# Revit family: Shower-Receptor-KOHLER-Bellwether-K-9178
name_source: partatom
category: Plumbing Fixtures
revit_build: Autodesk Revit 2015 (Build: 20140606_1530(x64)
units: mm (PartAtom-declared; Revit-internal decimal feet)

## types (6) — shared parameters
ADA Compliant = No
Assembly Code = C1030200
Date Modified = 09/12/2017
Default Elevation = 0"
Description = Bellwether 60inch x 34inch single-threshold shower base with right center drain
Flow Rate = 0 GPM
Height = 4 1/2"
Inlet Connector = Inlet Connection
Length = 60"
Manufacturer = KOHLER Co.
MasterFormat 1995 = 15410
MasterFormat 2004 = 22.41.23
Material = Enameled Cast Iron
Outlet Connector = Outlet Connection
Pressure = 0.00 psi
Product Documentation Link = http://www.us.kohler.com
Product Name = Bellwether
Product Page URL = http://www.us.kohler.com
URL = http://www.us.kohler.com
Waste Connection = Yes
Width = 34"

## per-type parameters (varying)
| type | Finish | Model | Type |
| 0-White | Kohler-Enameled_Cast_Iron-0-White | K-9178-0 | 1 |
| 96-Biscuit | Kohler-Enameled_Cast_Iron-96-Biscuit | K-9178-96 | 2 |
| 47-Almond | Kohler-Enameled_Cast_Iron-47-Almond | K-9178-47 | 3 |
| NY-Dune | Kohler-Enameled_Cast_Iron-NY-Dune | K-9178-NY | 4 |
| 95-Ice Grey | Kohler-Enameled_Cast_Iron-95-Ice_Grey | K-9178-95 | 5 |
| G9-Sandbar | Kohler-Enameled_Cast_Iron-G9-Sandbar | K-9178-G9 | 6 |

## geometry (parser evidence)
native form markers: Sweep x6
no freeform markers — native parametric forms only
